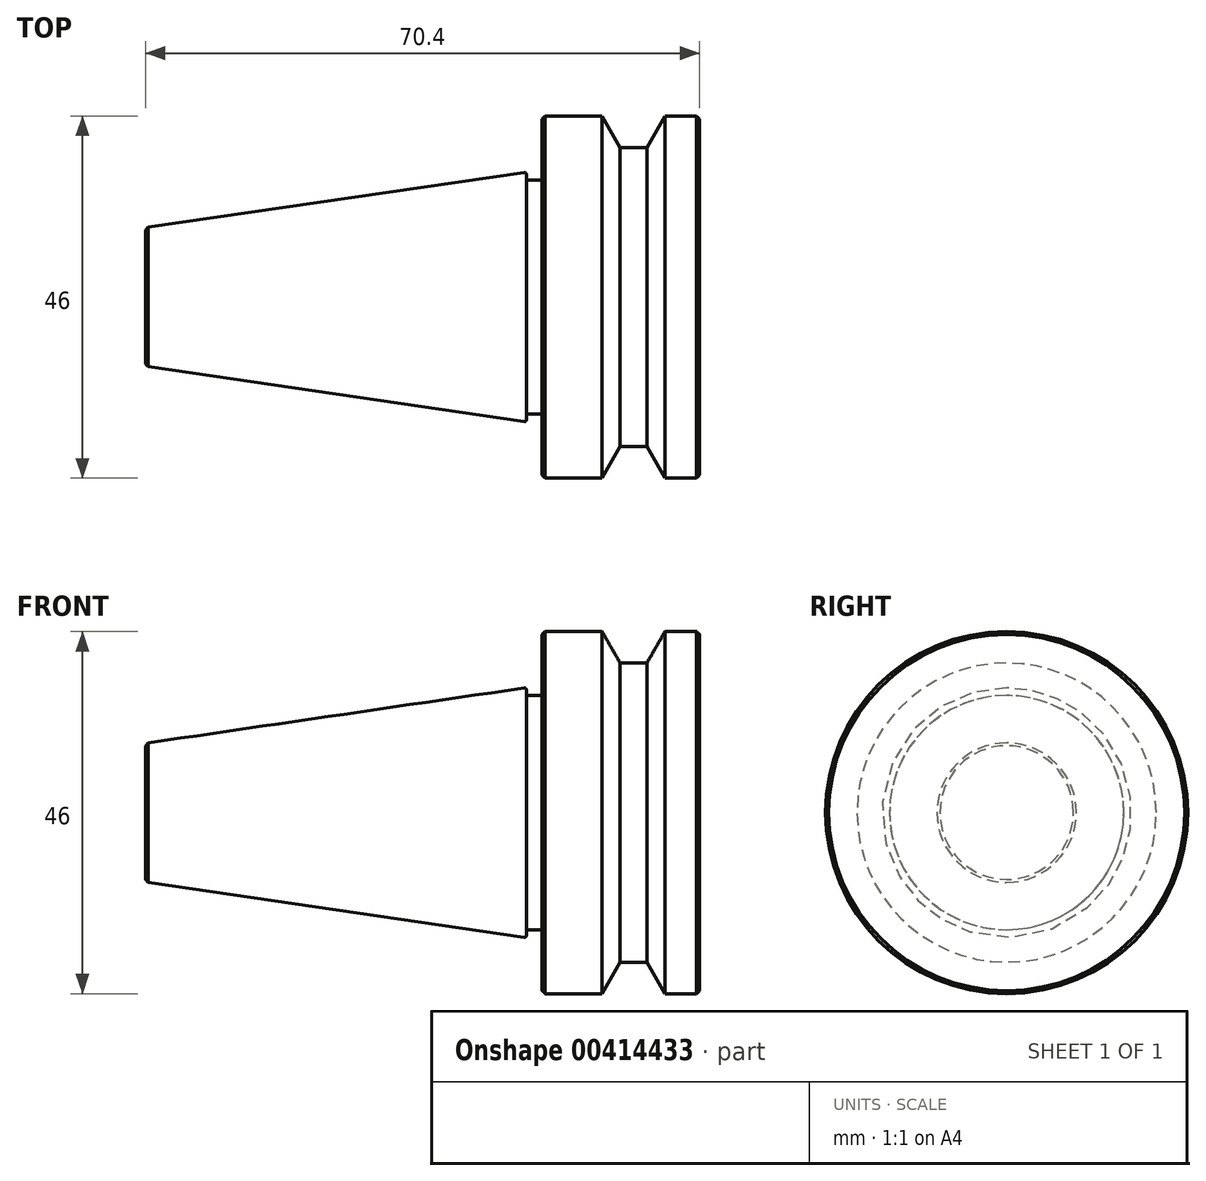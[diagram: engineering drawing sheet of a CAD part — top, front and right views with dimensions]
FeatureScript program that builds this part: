
annotation { "Feature Type Name" : "Feature", "Feature Type Description" : "" }
export const myFeature = defineFeature(function(context is Context, id is Id, definition is map)
    precondition{}
    {
        {
            var Q0;
            Q0=qCreatedBy(makeId("Top.planeOp"),FACE);
            var sketch = newSketch(context, id + "F0", { "sketchPlane" : qUnion([Q0])});
            skLineSegment(sketch, "E0", {"start": v(0, 0) * mm, "end": v(0, 23) * mm});
            skLineSegment(sketch, "E1", {"start": v(0, 23) * mm, "end": v(-4.4, 23) * mm});
            skLineSegment(sketch, "E2", {"start": v(-4.4, 23) * mm, "end": v(-6.7, 19) * mm});
            skLineSegment(sketch, "E3", {"start": v(-6.7, 19) * mm, "end": v(-10.1, 19) * mm});
            skLineSegment(sketch, "E4", {"start": v(-10.1, 19) * mm, "end": v(-12.4, 23) * mm});
            skLineSegment(sketch, "E5", {"start": v(-12.4, 23) * mm, "end": v(-20, 23) * mm});
            skLineSegment(sketch, "E6", {"start": v(-20, 23) * mm, "end": v(-20, 14.88) * mm});
            skLineSegment(sketch, "E7", {"start": v(-20, 14.88) * mm, "end": v(-22, 14.88) * mm});
            skLineSegment(sketch, "E8", {"start": v(-22, 14.88) * mm, "end": v(-22, 15.88) * mm});
            skLineSegment(sketch, "E9", {"start": v(-22, 15.88) * mm, "end": v(-70.4, 8.81) * mm});
            skLineSegment(sketch, "E10", {"start": v(-70.4, 8.81) * mm, "end": v(-70.4, 0) * mm});
            skLineSegment(sketch, "E11", {"start": v(-70.4, 0) * mm, "end": v(0, 0) * mm});
            skSolve(sketch);
        }
        {
            var Q0;
            Q0 = qSketchRegion(id + "F0", true);
            var Q1;
            Q1=sQuery(id+"F0.wireOp",EDGE,"E11");
            revolve(context, id + "F1", {"entities" : qUnion([Q0]), "axis" : qUnion([Q1]), "revolveType" : RevolveType.FULL});
        }
        {
            var Q0;
            Q0=makeQuery(id+"F1.opRevolve","SWEPT_EDGE",EDGE,{"disambiguationData":[OSD([sQuery(id+"F0.wireOp",EDGE,"E0"),sQuery(id+"F0.wireOp",EDGE,"E1")])]});
            var Q1;
            Q1=makeQuery(id+"F1.opRevolve","SWEPT_EDGE",EDGE,{"disambiguationData":[OSD([sQuery(id+"F0.wireOp",EDGE,"E5"),sQuery(id+"F0.wireOp",EDGE,"E6")])]});
            var Q2;
            Q2=makeQuery(id+"F1.opRevolve","SWEPT_EDGE",EDGE,{"disambiguationData":[OSD([sQuery(id+"F0.wireOp",EDGE,"E9"),sQuery(id+"F0.wireOp",EDGE,"E10")])]});
            chamfer(context, id + "F2", {"entities" : qUnion([Q0, Q1, Q2]), "width" : 0.38 * mm, "tangentPropagation" : true});
        }
        {
            var Q0;
            Q0=makeQuery(id+"F1.opRevolve","SWEPT_EDGE",EDGE,{"disambiguationData":[OSD([sQuery(id+"F0.wireOp",EDGE,"E8"),sQuery(id+"F0.wireOp",EDGE,"E9")])]});
            var Q1;
            Q1=makeQuery(id+"F1.opRevolve","SWEPT_FACE",FACE,{"disambiguationData":[OSD([sQuery(id+"F0.wireOp",EDGE,"E8")])]});
            var Q2;
            Q2=makeQuery(id+"F1.opRevolve","SWEPT_EDGE",EDGE,{"disambiguationData":[OSD([sQuery(id+"F0.wireOp",EDGE,"E6"),sQuery(id+"F0.wireOp",EDGE,"E7")])]});
            fillet(context, id + "F3", {"entities" : qUnion([Q0, Q1, Q2]), "radius" : 0.25 * mm, "tangentPropagation" : true, "allowEdgeOverflow" : false});
        }
    });
